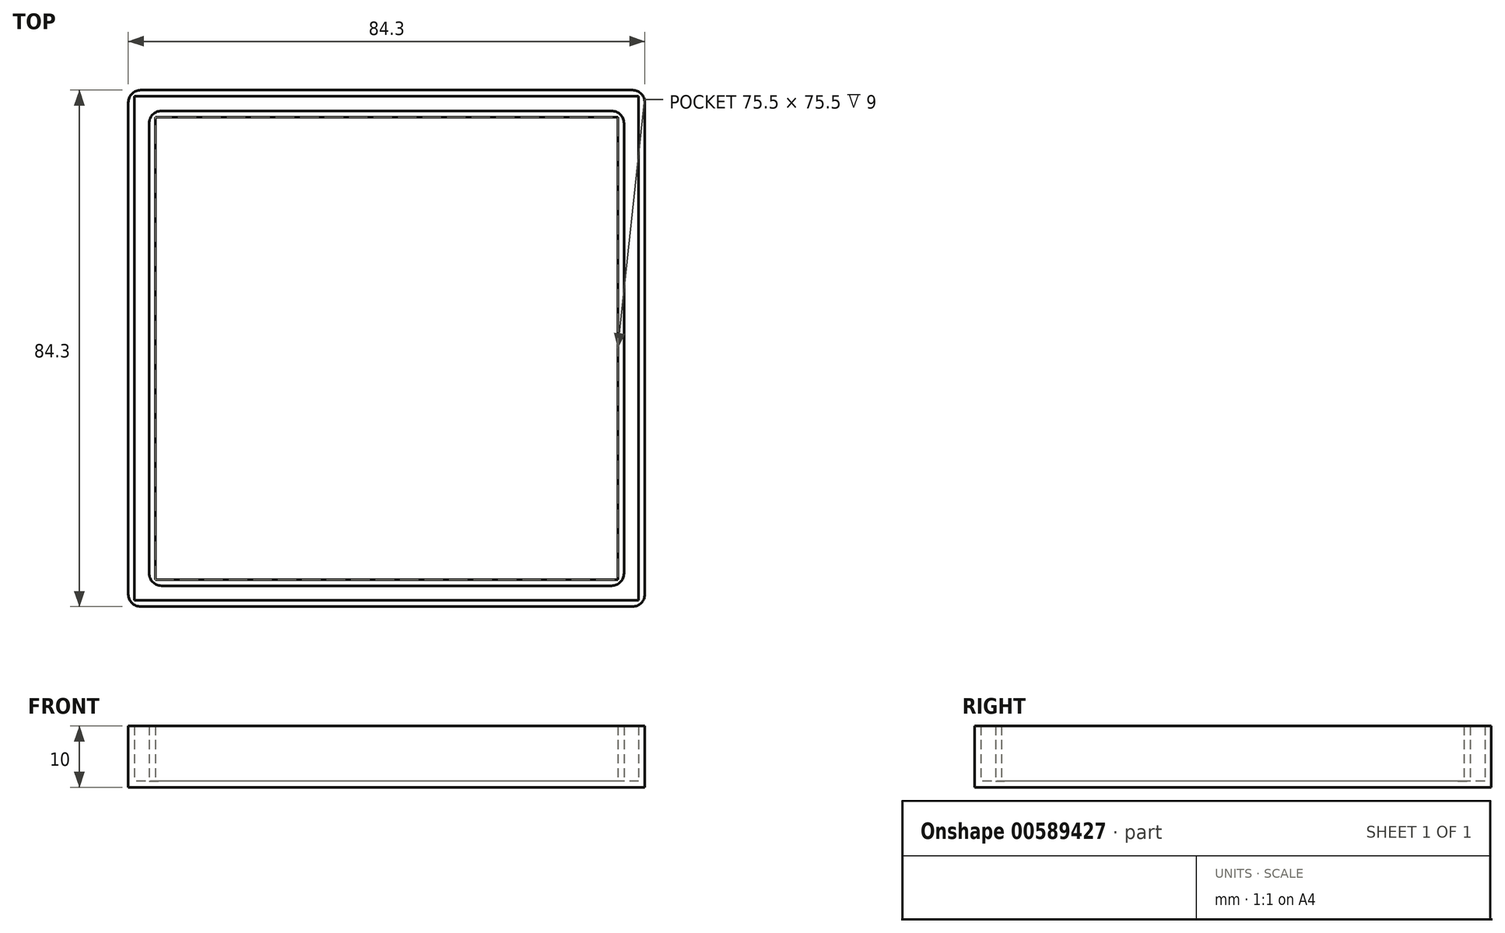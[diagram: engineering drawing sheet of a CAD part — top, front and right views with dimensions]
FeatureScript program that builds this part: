
annotation { "Feature Type Name" : "Feature", "Feature Type Description" : "" }
export const myFeature = defineFeature(function(context is Context, id is Id, definition is map)
    precondition{}
    {
        {
            var Q0;
            Q0=qCreatedBy(makeId("Top.planeOp"),FACE);
            var sketch = newSketch(context, id + "F0", { "sketchPlane" : qUnion([Q0])});
            skLineSegment(sketch, "E0.bottom", {"start": v(41.15, 41.15) * mm, "end": v(-41.15, 41.15) * mm});
            skLineSegment(sketch, "E0.top", {"start": v(41.15, -41.15) * mm, "end": v(-41.15, -41.15) * mm});
            skLineSegment(sketch, "E0.left", {"start": v(41.15, 41.15) * mm, "end": v(41.15, -41.15) * mm});
            skLineSegment(sketch, "E0.right", {"start": v(-41.15, 41.15) * mm, "end": v(-41.15, -41.15) * mm});
            skPoint(sketch, "E0.middle", {"position": v(0, 0) * mm});
            skLineSegment(sketch, "E1.0", {"start": v(40.15, 42.15) * mm, "end": v(-40.15, 42.15) * mm});
            skLineSegment(sketch, "E1.1", {"start": v(42.15, 40.15) * mm, "end": v(42.15, -40.15) * mm});
            skLineSegment(sketch, "E1.2", {"start": v(40.15, -42.15) * mm, "end": v(-40.15, -42.15) * mm});
            skLineSegment(sketch, "E1.3", {"start": v(-42.15, 40.15) * mm, "end": v(-42.15, -40.15) * mm});
            skLineSegment(sketch, "E2.0", {"start": v(-38.75, 36.75) * mm, "end": v(-38.75, -36.75) * mm});
            skLineSegment(sketch, "E2.1", {"start": v(36.75, 38.75) * mm, "end": v(-36.75, 38.75) * mm});
            skLineSegment(sketch, "E2.2", {"start": v(38.75, 36.75) * mm, "end": v(38.75, -36.75) * mm});
            skLineSegment(sketch, "E2.3", {"start": v(36.75, -38.75) * mm, "end": v(-36.75, -38.75) * mm});
            skLineSegment(sketch, "E3.0", {"start": v(-37.75, 37.75) * mm, "end": v(-37.75, -37.75) * mm});
            skLineSegment(sketch, "E3.1", {"start": v(37.75, 37.75) * mm, "end": v(-37.75, 37.75) * mm});
            skLineSegment(sketch, "E3.2", {"start": v(37.75, 37.75) * mm, "end": v(37.75, -37.75) * mm});
            skLineSegment(sketch, "E3.3", {"start": v(37.75, -37.75) * mm, "end": v(-37.75, -37.75) * mm});
            skPoint(sketch, "E4.visualSharp", {"position": v(-42.15, 42.15) * mm});
            skArc(sketch, "E4.filletArc", {"start": v(-40.15, 42.15) * mm, "mid": v(-41.56, 41.56) * mm, "end": v(-42.15, 40.15) * mm});
            skPoint(sketch, "E5.visualSharp", {"position": v(-38.75, 38.75) * mm});
            skArc(sketch, "E5.filletArc", {"start": v(-36.75, 38.75) * mm, "mid": v(-38.16, 38.16) * mm, "end": v(-38.75, 36.75) * mm});
            skPoint(sketch, "E6.visualSharp", {"position": v(38.75, 38.75) * mm});
            skArc(sketch, "E6.filletArc", {"start": v(38.75, 36.75) * mm, "mid": v(38.16, 38.16) * mm, "end": v(36.75, 38.75) * mm});
            skPoint(sketch, "E7.visualSharp", {"position": v(38.75, -38.75) * mm});
            skArc(sketch, "E7.filletArc", {"start": v(36.75, -38.75) * mm, "mid": v(38.16, -38.16) * mm, "end": v(38.75, -36.75) * mm});
            skPoint(sketch, "E8.visualSharp", {"position": v(42.15, -42.15) * mm});
            skArc(sketch, "E8.filletArc", {"start": v(40.15, -42.15) * mm, "mid": v(41.56, -41.56) * mm, "end": v(42.15, -40.15) * mm});
            skPoint(sketch, "E9.visualSharp", {"position": v(-42.15, -42.15) * mm});
            skArc(sketch, "E9.filletArc", {"start": v(-42.15, -40.15) * mm, "mid": v(-41.56, -41.56) * mm, "end": v(-40.15, -42.15) * mm});
            skPoint(sketch, "E10.visualSharp", {"position": v(-38.75, -38.75) * mm});
            skArc(sketch, "E10.filletArc", {"start": v(-38.75, -36.75) * mm, "mid": v(-38.16, -38.16) * mm, "end": v(-36.75, -38.75) * mm});
            skPoint(sketch, "E11.visualSharp", {"position": v(42.15, 42.15) * mm});
            skArc(sketch, "E11.filletArc", {"start": v(42.15, 40.15) * mm, "mid": v(41.56, 41.56) * mm, "end": v(40.15, 42.15) * mm});
            skSolve(sketch);
        }
        {
            var Q0;
            Q0 = qSketchRegion(id + "F0", true);
            var Q1;
            Q1=makeQuery(id+"F0.imprint","IMPRINT",FACE,{"disambiguationData":[TD([[makeQuery(id+"F0.imprint","IMPRINT",EDGE,{"derivedFrom":sQuery(id+"F0.wireOp",EDGE,"E2.0")}),1.0]])]});
            extrude(context, id + "F1", {"entities" : qUnion([Q0, Q1]), "depth" : 10 * mm, "offsetDistance" : 25 * mm});
        }
        {
            var Q0;
            Q0=makeQuery(id+"F0.imprint","IMPRINT",FACE,{"disambiguationData":[TD([[makeQuery(id+"F0.imprint","IMPRINT",EDGE,{"derivedFrom":sQuery(id+"F0.wireOp",EDGE,"E0.bottom")}),1.0]])]});
            var Q1;
            Q1=makeQuery(id+"F0.imprint","IMPRINT",FACE,{"disambiguationData":[TD([[makeQuery(id+"F0.imprint","IMPRINT",EDGE,{"derivedFrom":sQuery(id+"F0.wireOp",EDGE,"E3.0")}),1.0]])]});
            extrude(context, id + "F2", {"entities" : qUnion([Q0, Q1]), "operationType" : NewBodyOperationType.ADD, "depth" : 1 * mm, "offsetDistance" : 25 * mm});
        }
    });
